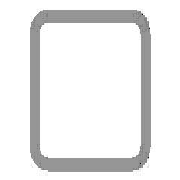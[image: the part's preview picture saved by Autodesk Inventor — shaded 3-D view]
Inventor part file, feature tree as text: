
AUTODESK INVENTOR PART (.ipt)
format: ipt  version: 2022 (Build 260153000, 153)  size: 154,112 bytes
history: native  units: mm (DEFAULTED — no unit token found)
features: other x4, plane x3, sketch x3, split x2, extrude x1
ambient origin geometry x8: Origin, YZ Plane, XZ Plane, XY Plane, X Axis, Y Axis, Z Axis, Center Point
bodies: Solid1 (feature_tree)
feature tree (13):
  parser-record x1  (decoder bookkeeping rows leaked as tree rows — omitted from the tree; the rows remain in map.json)
  other  "Driven Length"
  other  "Plano inicial"
  other  "Plano final"
  extrude  "Cuerpo"  TaperAngle=0.0deg  [1 undecoded]
  plane  "Plano de trabajo4"
  split  "Dividir1"
  plane  "Plano de trabajo5"
  split  "Dividir2"
  sketch  "Boceto"  dims[d10=40.0mm d11=40.0mm d12=5.0mm d13=-5.182521mm d14=320.0mm d15=20.0mm d16=20.0mm d17=90.0deg d18=325.182521mm]
  sketch  "Sketch3"  dims[d3=325.182521mm d4=0.0mm]
  plane  "Work Plane3"
  sketch  "Sketch4"  dims[d7=7.5mm]
note: 1 required parameter value undecoded (feature->parameter linkage not recoverable at this tier; creation-order binding heuristic only, values carry confidence <= 0.55)
